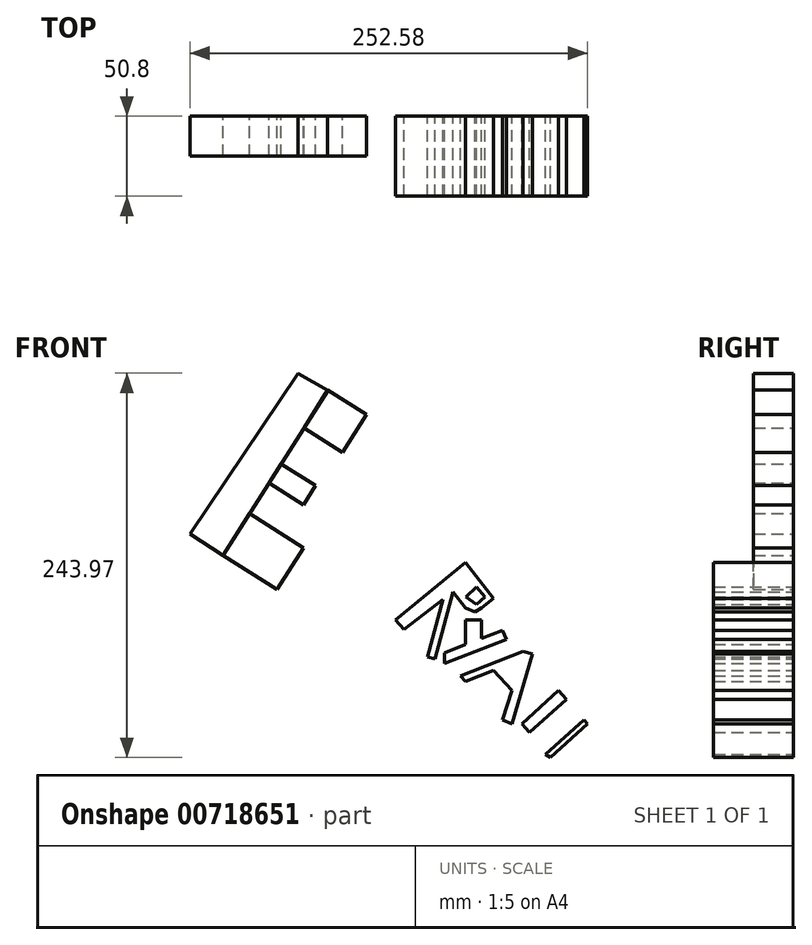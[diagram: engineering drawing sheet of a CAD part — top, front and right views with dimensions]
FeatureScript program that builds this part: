
annotation { "Feature Type Name" : "Feature", "Feature Type Description" : "" }
export const myFeature = defineFeature(function(context is Context, id is Id, definition is map)
    precondition{}
    {
        {
            var Q0;
            Q0=qCreatedBy(makeId("Front.planeOp"),FACE);
            var sketch = newSketch(context, id + "F0", { "sketchPlane" : qUnion([Q0])});
            skLineSegment(sketch, "E0", {"start": v(-134.28, 32.1) * mm, "end": v(-200.77, -72.81) * mm});
            skLineSegment(sketch, "E1", {"start": v(-134.28, 32.1) * mm, "end": v(-109.8, 16.58) * mm});
            skLineSegment(sketch, "E2", {"start": v(-200.77, -72.81) * mm, "end": v(-166.57, -94.49) * mm});
            skLineSegment(sketch, "E3", {"start": v(-166.57, -94.49) * mm, "end": v(-149.77, -67.97) * mm});
            skLineSegment(sketch, "E4", {"start": v(-149.77, -67.97) * mm, "end": v(-183.97, -46.3) * mm});
            skLineSegment(sketch, "E5", {"start": v(-109.8, 16.58) * mm, "end": v(-124.96, -7.36) * mm});
            skLineSegment(sketch, "E6", {"start": v(-124.96, -7.36) * mm, "end": v(-149.77, 8.37) * mm});
            skLineSegment(sketch, "E7", {"start": v(-171.6, -26.78) * mm, "end": v(-149.77, -40.61) * mm});
            skLineSegment(sketch, "E8", {"start": v(-149.77, -40.61) * mm, "end": v(-142.06, -28.45) * mm});
            skLineSegment(sketch, "E9", {"start": v(-142.06, -28.45) * mm, "end": v(-163.89, -14.62) * mm});
            skSolve(sketch);
        }
        {
            var Q0;
            Q0=qCreatedBy(makeId("Front.planeOp"),FACE);
            var sketch = newSketch(context, id + "F1", { "sketchPlane" : qUnion([Q0])});
            skLineSegment(sketch, "E10", {"start": v(-134.14, 31.92) * mm, "end": v(-153.23, 42.89) * mm});
            skLineSegment(sketch, "E11", {"start": v(-153.23, 42.89) * mm, "end": v(-221.83, -59.08) * mm});
            skLineSegment(sketch, "E12", {"start": v(-200.75, -72.88) * mm, "end": v(-221.83, -59.08) * mm});
            skLineSegment(sketch, "E13", {"start": v(-200.75, -72.88) * mm, "end": v(-134.14, 31.92) * mm});
            skSolve(sketch);
        }
        {
            var Q0;
            Q0=makeQuery(id+"F1.imprint","IMPRINT",FACE,{"disambiguationData":[TD([[makeQuery(id+"F1.imprint","IMPRINT",EDGE,{"derivedFrom":sQuery(id+"F1.wireOp",EDGE,"E10")}),1.0]])]});
            var Q1;
            {var subQ0=sQuery(id+"F0.wireOp",EDGE,"E1");Q1=makeQuery(id+"F0.imprint","IMPRINT",FACE,{"disambiguationData":[TD([[makeQuery(id+"F0.imprint","IMPRINT",EDGE,{"derivedFrom":subQ0}),-1.0]])]});}
            var Q2;
            {var subQ0=sQuery(id+"F0.wireOp",EDGE,"E7");Q2=makeQuery(id+"F0.imprint","IMPRINT",FACE,{"disambiguationData":[TD([[makeQuery(id+"F0.imprint","IMPRINT",EDGE,{"derivedFrom":subQ0}),1.0]])]});}
            var Q3;
            {var subQ0=sQuery(id+"F0.wireOp",EDGE,"E2");Q3=makeQuery(id+"F0.imprint","IMPRINT",FACE,{"disambiguationData":[TD([[makeQuery(id+"F0.imprint","IMPRINT",EDGE,{"derivedFrom":subQ0}),1.0]])]});}
            extrude(context, id + "F2", {"entities" : qUnion([Q0, Q1, Q2, Q3]), "depth" : 25.4 * mm, "offsetDistance" : 25.4 * mm});
        }
        {
            var Q0;
            Q0=qCreatedBy(makeId("Front.planeOp"),FACE);
            var sketch = newSketch(context, id + "F3", { "sketchPlane" : qUnion([Q0])});
            skLineSegment(sketch, "E14", {"start": v(-40.75, -85) * mm, "end": v(-85.78, -119.97) * mm});
            skLineSegment(sketch, "E15", {"start": v(-40.75, -85) * mm, "end": v(-28.88, -100.28) * mm});
            skLineSegment(sketch, "E16", {"start": v(-28.88, -100.28) * mm, "end": v(-36.58, -106.26) * mm});
            skLineSegment(sketch, "E17", {"start": v(-40.75, -108.74) * mm, "end": v(-36.58, -106.26) * mm});
            skLineSegment(sketch, "E18", {"start": v(-40.75, -108.74) * mm, "end": v(-46.82, -106.26) * mm});
            skLineSegment(sketch, "E19", {"start": v(-46.82, -106.26) * mm, "end": v(-54.84, -95.93) * mm});
            skLineSegment(sketch, "E20", {"start": v(-54.84, -95.93) * mm, "end": v(-66.24, -138.49) * mm});
            skLineSegment(sketch, "E21", {"start": v(-20.68, -126.13) * mm, "end": v(-60.1, -141.57) * mm});
            skLineSegment(sketch, "E22", {"start": v(-60.1, -141.57) * mm, "end": v(-60.1, -134.68) * mm});
            skLineSegment(sketch, "E23", {"start": v(-60.1, -134.68) * mm, "end": v(-23.42, -120.31) * mm});
            skLineSegment(sketch, "E24", {"start": v(-23.42, -120.31) * mm, "end": v(-20.68, -126.13) * mm});
            skLineSegment(sketch, "E25", {"start": v(-46.82, -129.47) * mm, "end": v(-46.82, -120.31) * mm});
            skLineSegment(sketch, "E26", {"start": v(-46.82, -120.31) * mm, "end": v(-46.82, -113.94) * mm});
            skLineSegment(sketch, "E27", {"start": v(-46.82, -113.94) * mm, "end": v(-36.58, -113.94) * mm});
            skLineSegment(sketch, "E28", {"start": v(-36.58, -113.94) * mm, "end": v(-36.58, -125.47) * mm});
            skLineSegment(sketch, "E29", {"start": v(-40.75, -85) * mm, "end": v(-46.82, -77.19) * mm});
            skLineSegment(sketch, "E30", {"start": v(-46.82, -77.19) * mm, "end": v(-91.25, -113.94) * mm});
            skLineSegment(sketch, "E31", {"start": v(-85.78, -119.97) * mm, "end": v(-91.25, -113.94) * mm});
            skLineSegment(sketch, "E32", {"start": v(-66.24, -138.49) * mm, "end": v(-70.9, -137.24) * mm});
            skLineSegment(sketch, "E33", {"start": v(-70.9, -137.24) * mm, "end": v(-60.1, -96.93) * mm});
            skLineSegment(sketch, "E34", {"start": v(-60.1, -96.93) * mm, "end": v(-54.84, -95.93) * mm});
            skLineSegment(sketch, "E35", {"start": v(-10.3, -138.49) * mm, "end": v(-46.82, -152.79) * mm});
            skLineSegment(sketch, "E36", {"start": v(-10.3, -138.49) * mm, "end": v(-23.42, -177.14) * mm});
            skLineSegment(sketch, "E37", {"start": v(-28.88, -145.76) * mm, "end": v(-17.16, -158.68) * mm});
            skLineSegment(sketch, "E38", {"start": v(-46.82, -152.79) * mm, "end": v(-49.98, -149.3) * mm});
            skLineSegment(sketch, "E39", {"start": v(-49.98, -149.3) * mm, "end": v(-10.3, -133.76) * mm});
            skLineSegment(sketch, "E40", {"start": v(-10.3, -133.76) * mm, "end": v(-10.3, -138.49) * mm});
            skLineSegment(sketch, "E41", {"start": v(-10.3, -133.76) * mm, "end": v(-4.14, -135.4) * mm});
            skLineSegment(sketch, "E42", {"start": v(-4.14, -135.4) * mm, "end": v(-17.16, -179.69) * mm});
            skLineSegment(sketch, "E43", {"start": v(-17.16, -179.69) * mm, "end": v(-23.42, -177.14) * mm});
            skLineSegment(sketch, "E44", {"start": v(12.25, -158.68) * mm, "end": v(-10.9, -179.69) * mm});
            skLineSegment(sketch, "E45", {"start": v(12.25, -158.68) * mm, "end": v(17.22, -164.16) * mm});
            skLineSegment(sketch, "E46", {"start": v(17.22, -164.16) * mm, "end": v(-6, -185.23) * mm});
            skLineSegment(sketch, "E47", {"start": v(-6, -185.23) * mm, "end": v(-10.9, -179.69) * mm});
            skLineSegment(sketch, "E48", {"start": v(17.22, -164.16) * mm, "end": v(7.32, -201.08) * mm});
            skLineSegment(sketch, "E49", {"start": v(17.22, -164.16) * mm, "end": v(12.25, -168.67) * mm});
            skLineSegment(sketch, "E50", {"start": v(12.25, -168.67) * mm, "end": v(4.05, -199.28) * mm});
            skLineSegment(sketch, "E51", {"start": v(7.32, -201.08) * mm, "end": v(4.05, -199.28) * mm});
            skLineSegment(sketch, "E52", {"start": v(4.05, -199.28) * mm, "end": v(28.44, -177.14) * mm});
            skLineSegment(sketch, "E53", {"start": v(28.44, -177.14) * mm, "end": v(30.75, -179.69) * mm});
            skLineSegment(sketch, "E54", {"start": v(30.75, -179.69) * mm, "end": v(7.32, -201.08) * mm});
            skSolve(sketch);
        }
        {
            var Q0;
            Q0=qCreatedBy(makeId("Front.planeOp"),FACE);
            var sketch = newSketch(context, id + "F4", { "sketchPlane" : qUnion([Q0])});
            skLineSegment(sketch, "E55", {"start": v(-39.93, -93) * mm, "end": v(-46.62, -99.08) * mm});
            skLineSegment(sketch, "E56", {"start": v(-39.93, -93) * mm, "end": v(-34.4, -99.08) * mm});
            skLineSegment(sketch, "E57", {"start": v(-34.4, -99.08) * mm, "end": v(-39.93, -104.1) * mm});
            skLineSegment(sketch, "E58", {"start": v(-39.93, -104.1) * mm, "end": v(-46.62, -99.08) * mm});
            skSolve(sketch);
        }
        {
            var Q0;
            Q0=makeQuery(id+"F3.imprint","IMPRINT",FACE,{"disambiguationData":[TD([[makeQuery(id+"F3.imprint","IMPRINT",EDGE,{"derivedFrom":sQuery(id+"F3.wireOp",EDGE,"E44")}),1.0]])]});
            var Q1;
            {var subQ0=sQuery(id+"F3.wireOp",EDGE,"E15");Q1=makeQuery(id+"F3.imprint","IMPRINT",FACE,{"disambiguationData":[TD([[makeQuery(id+"F3.imprint","IMPRINT",EDGE,{"derivedFrom":subQ0}),-1.0]])]});}
            var Q2;
            {var subQ0=sQuery(id+"F3.wireOp",EDGE,"E25");Q2=makeQuery(id+"F3.imprint","IMPRINT",FACE,{"disambiguationData":[TD([[makeQuery(id+"F3.imprint","IMPRINT",EDGE,{"derivedFrom":subQ0}),-1.0]])]});}
            var Q3;
            {var subQ0=sQuery(id+"F3.wireOp",EDGE,"E20");Q3=makeQuery(id+"F3.imprint","IMPRINT",FACE,{"disambiguationData":[TD([[makeQuery(id+"F3.imprint","IMPRINT",EDGE,{"derivedFrom":subQ0}),-1.0]])]});}
            var Q4;
            Q4=makeQuery(id+"F3.imprint","IMPRINT",FACE,{"disambiguationData":[TD([[makeQuery(id+"F3.imprint","IMPRINT",EDGE,{"derivedFrom":sQuery(id+"F3.wireOp",EDGE,"E21")}),-1.0]])]});
            var Q5;
            {var subQ0=sQuery(id+"F3.wireOp",EDGE,"E29");Q5=makeQuery(id+"F3.imprint","IMPRINT",FACE,{"disambiguationData":[TD([[makeQuery(id+"F3.imprint","IMPRINT",EDGE,{"derivedFrom":subQ0}),1.0]])]});}
            var Q6;
            {var subQ4=sQuery(id+"F3.wireOp",EDGE,"E53");Q6=makeQuery(id+"F3.imprint","IMPRINT",FACE,{"disambiguationData":[TD([[makeQuery(id+"F3.imprint","IMPRINT",EDGE,{"derivedFrom":subQ4}),-1.0]])]});}
            var Q7;
            {var subQ0=sQuery(id+"F3.wireOp",EDGE,"E38");Q7=makeQuery(id+"F3.imprint","IMPRINT",FACE,{"disambiguationData":[TD([[makeQuery(id+"F3.imprint","IMPRINT",EDGE,{"derivedFrom":subQ0}),-1.0]])]});}
            var Q8;
            {var subQ3=sQuery(id+"F3.wireOp",EDGE,"E37");Q8=makeQuery(id+"F3.imprint","IMPRINT",FACE,{"disambiguationData":[TD([[makeQuery(id+"F3.imprint","IMPRINT",EDGE,{"derivedFrom":subQ3}),1.0]])]});}
            var Q9;
            {var subQ3=sQuery(id+"F3.wireOp",EDGE,"E40");Q9=makeQuery(id+"F3.imprint","IMPRINT",FACE,{"disambiguationData":[TD([[makeQuery(id+"F3.imprint","IMPRINT",EDGE,{"derivedFrom":subQ3}),1.0]])]});}
            var Q10;
            {var subQ0=sQuery(id+"F3.wireOp",EDGE,"E49");Q10=makeQuery(id+"F3.imprint","IMPRINT",FACE,{"disambiguationData":[TD([[makeQuery(id+"F3.imprint","IMPRINT",EDGE,{"derivedFrom":subQ0}),1.0]])]});}
            var Q11;
            {var subQ0=sQuery(id+"F3.wireOp",EDGE,"E51");Q11=makeQuery(id+"F3.imprint","IMPRINT",FACE,{"disambiguationData":[TD([[makeQuery(id+"F3.imprint","IMPRINT",EDGE,{"derivedFrom":subQ0}),-1.0]])]});}
            var Q12;
            Q12=makeQuery(id+"F4.imprint","IMPRINT",FACE,{"disambiguationData":[TD([[makeQuery(id+"F4.imprint","IMPRINT",EDGE,{"derivedFrom":sQuery(id+"F4.wireOp",EDGE,"E55")}),1.0]])]});
            var Q13;
            {var subQ0=sQuery(id+"F3.wireOp",EDGE,"E34");Q13=makeQuery(id+"F3.imprint","IMPRINT",FACE,{"disambiguationData":[TD([[makeQuery(id+"F3.imprint","IMPRINT",EDGE,{"derivedFrom":subQ0}),-1.0]])]});}
            extrude(context, id + "F5", {"entities" : qUnion([Q0, Q1, Q2, Q3, Q4, Q5, Q6, Q7, Q8, Q9, Q10, Q11, Q12, Q13]), "depth" : 50.8 * mm, "offsetDistance" : 25.4 * mm});
        }
    });
